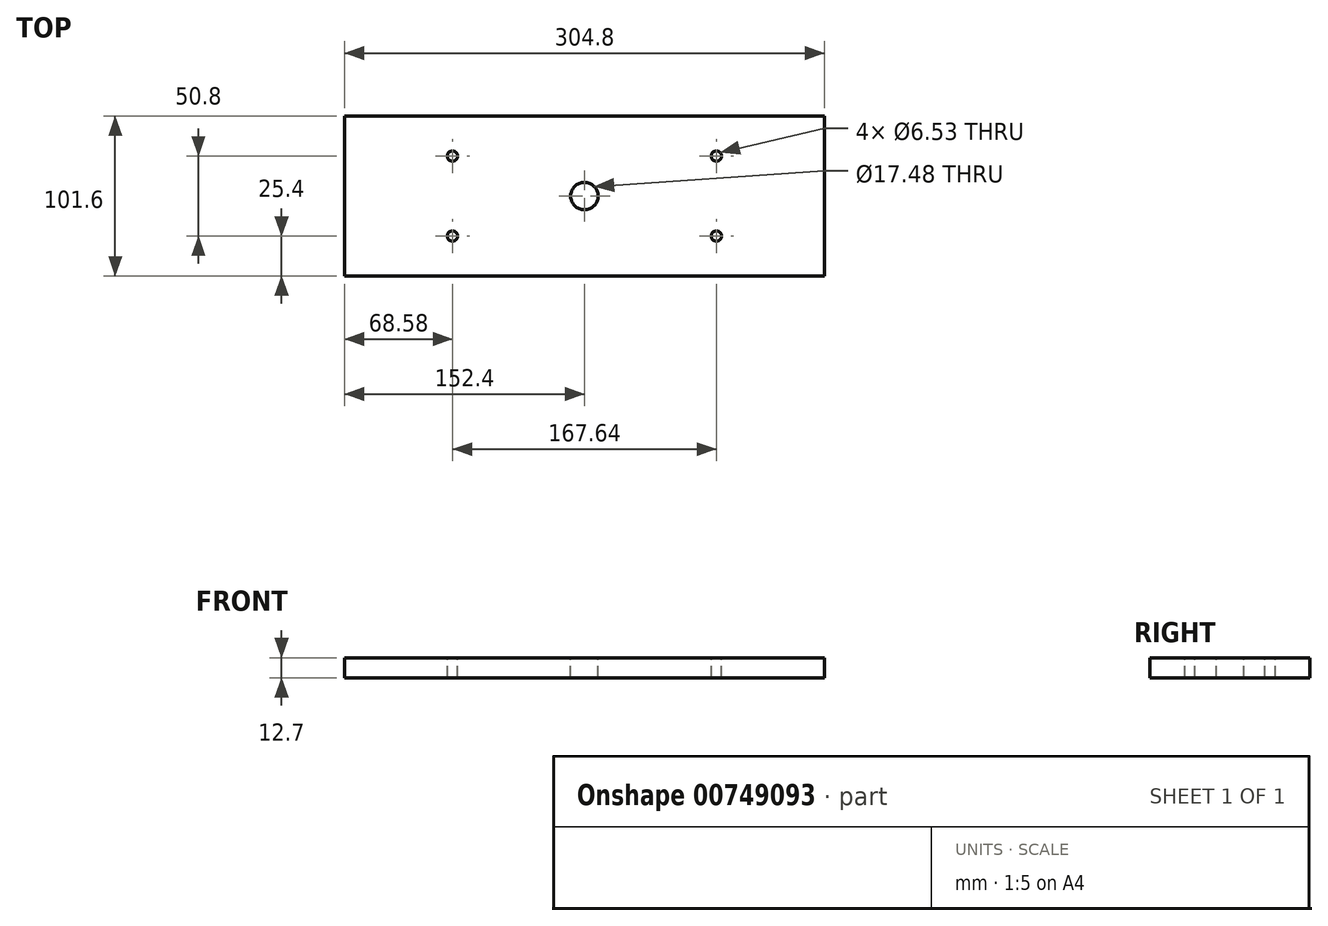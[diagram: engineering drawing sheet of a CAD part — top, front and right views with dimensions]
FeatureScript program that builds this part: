
annotation { "Feature Type Name" : "Feature", "Feature Type Description" : "" }
export const myFeature = defineFeature(function(context is Context, id is Id, definition is map)
    precondition{}
    {
        {
            var Q0;
            Q0=qCreatedBy(makeId("Top.planeOp"),FACE);
            var sketch = newSketch(context, id + "F0", { "sketchPlane" : qUnion([Q0])});
            skLineSegment(sketch, "E0.bottom", {"start": v(0, 0) * mm, "end": v(304.8, 0) * mm});
            skLineSegment(sketch, "E0.top", {"start": v(0, 101.6) * mm, "end": v(304.8, 101.6) * mm});
            skLineSegment(sketch, "E0.left", {"start": v(0, 0) * mm, "end": v(0, 101.6) * mm});
            skLineSegment(sketch, "E0.right", {"start": v(304.8, 0) * mm, "end": v(304.8, 101.6) * mm});
            skLineSegment(sketch, "E1", {"start": v(0, 50.8) * mm, "end": v(304.8, 50.8) * mm, "construction": true});
            skLineSegment(sketch, "E2", {"start": v(152.4, 0) * mm, "end": v(152.4, 101.6) * mm, "construction": true});
            skPoint(sketch, "E3", {"position": v(152.4, 50.8) * mm});
            skPoint(sketch, "E4", {"position": v(68.58, 76.2) * mm});
            skPoint(sketch, "E5.MirrorP", {"position": v(68.58, 25.4) * mm});
            skPoint(sketch, "E6.MirrorP", {"position": v(236.22, 76.2) * mm});
            skPoint(sketch, "E7.MirrorP", {"position": v(236.22, 25.4) * mm});
            skSolve(sketch);
        }
        {
            var Q0;
            Q0 = qSketchRegion(id + "F0", true);
            extrude(context, id + "F1", {"entities" : qUnion([Q0]), "depth" : 12.7 * mm, "offsetDistance" : 25.4 * mm});
        }
        {
            var Q0;
            Q0=sQuery(id+"F0.wireOp",VERTEX,"E4");
            var Q1;
            Q1=sQuery(id+"F0.wireOp",VERTEX,"E5.MirrorP");
            var Q2;
            Q2=sQuery(id+"F0.wireOp",VERTEX,"E6.MirrorP");
            var Q3;
            Q3=sQuery(id+"F0.wireOp",VERTEX,"E7.MirrorP");
            var Q4;
            Q4=makeQuery(id+"F1.opExtrude","SWEPT_BODY",BODY,{"disambiguationData":[OSD([sQuery(id+"F0.wireOp",EDGE,"E0.bottom"),sQuery(id+"F0.wireOp",EDGE,"E0.top"),sQuery(id+"F0.wireOp",EDGE,"E0.left"),sQuery(id+"F0.wireOp",EDGE,"E0.right")])]});
            hole(context, id + "F2", {"style" : HoleStyle.SIMPLE, "endStyle" : HoleEndStyle.BLIND, "oppositeDirection" : true, "standardTappedOrClearance" : lookupTablePath({ "standard" : "ANSI", "engagement" : "75%", "pitch" : "18 tpi", "size" : "5/16", "type" : "Tapped" }), "standardBlindInLast" : lookupTablePath({ "standard" : "ANSI", "engagement" : "75%", "pitch" : "18 tpi", "size" : "5/16", "type" : "Tapped" }), "holeDiameter" : 6.53 * mm, "majorDiameter" : 7.94 * mm, "showTappedDepth" : true, "holeDepth" : 16.95 * mm, "isTappedThrough" : true, "tappedDepth" : 12.71 * mm, "tapClearance" : 3, "locations" : qUnion([Q0, Q1, Q2, Q3]), "scope" : qUnion([Q4])});
        }
        {
            var Q0;
            Q0=sQuery(id+"F0.wireOp",VERTEX,"E3");
            var Q1;
            Q1=makeQuery(id+"F1.opExtrude","SWEPT_BODY",BODY,{"disambiguationData":[OSD([sQuery(id+"F0.wireOp",EDGE,"E0.bottom"),sQuery(id+"F0.wireOp",EDGE,"E0.top"),sQuery(id+"F0.wireOp",EDGE,"E0.left"),sQuery(id+"F0.wireOp",EDGE,"E0.right")])]});
            hole(context, id + "F3", {"style" : HoleStyle.SIMPLE, "endStyle" : HoleEndStyle.BLIND, "oppositeDirection" : true, "standardTappedOrClearance" : lookupTablePath({ "fit" : "Normal (ASME)", "standard" : "ANSI", "size" : "5/8", "type" : "Clearance" }), "standardBlindInLast" : lookupTablePath({ "fit" : "Normal", "standard" : "ANSI", "size" : "5/8", "type" : "Clearance" }), "holeDiameter" : 17.48 * mm, "majorDiameter" : 15.88 * mm, "holeDepth" : 16.94 * mm, "isTappedThrough" : true, "tappedDepth" : 12.7 * mm, "tapClearance" : 3, "locations" : qUnion([Q0]), "scope" : qUnion([Q1])});
        }
    });
